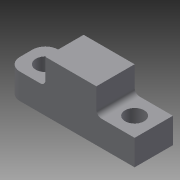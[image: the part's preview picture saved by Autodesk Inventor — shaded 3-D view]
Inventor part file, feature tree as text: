
AUTODESK INVENTOR PART (.ipt)
format: ipt  version: 2015 (Build 190159000, 159)  size: 115,712 bytes
history: native  units: in
note: dims shown in document units (in); Inventor stores cm internally (conversion verified against a paired STEP export)
features: sketch x4, fillet x3, extrude x2, hole x2
ambient origin geometry x8: Origin, YZ Plane, XZ Plane, XY Plane, X Axis, Y Axis, Z Axis, Center Point
bodies: Solid1 (feature_tree)
feature tree (11):
  extrude  "Extrusion1"  Depth=0.5in
  fillet  "Fillet1"  Radius=0.5in
  hole  "Hole1"  [1 undecoded]
  extrude  "Extrusion3"  Depth=0.1in
  hole  "Hole2"  [1 undecoded]
  fillet  "Fillet4"  Radius=0.75in
  fillet  "Fillet5"  Radius=0.1in
  sketch  "Sketch1"  dims[d1=0.5in d2=1.25in d3=0.5in]
  sketch  "Sketch2"  dims[d4=0.75in d5=0.0in d6=0.25in]
  sketch  "Sketch4"  dims[d8=0.375in]
  sketch  "Sketch6"  dims[d9=0.375in d10=0.75in d11=0.375in d12=0.25in d13=0.5635in d14=1.0in d15=0.8108in d16=1.25in d17=0.5in d21=0.75in d22=0.0in d26=0.375in d27=0.75in d28=0.375in d29=0.25in d30=0.5635in d31=1.0in d32=0.8108in d39=0.1in d40=0.1in]
note: 2 required parameter values undecoded (feature->parameter linkage not recoverable at this tier; creation-order binding heuristic only, values carry confidence <= 0.55)
